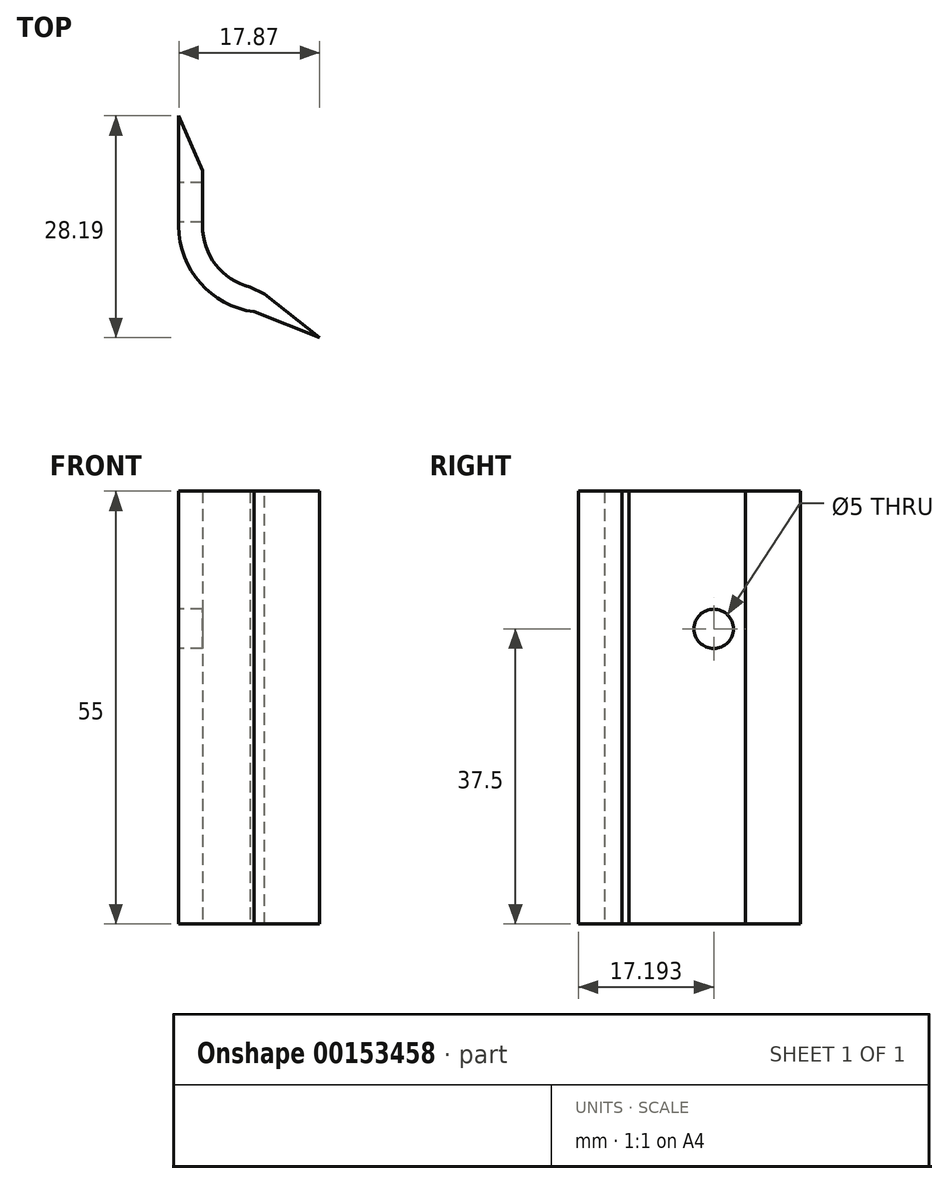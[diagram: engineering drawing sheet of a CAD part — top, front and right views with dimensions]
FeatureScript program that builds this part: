
annotation { "Feature Type Name" : "Feature", "Feature Type Description" : "" }
export const myFeature = defineFeature(function(context is Context, id is Id, definition is map)
    precondition{}
    {
        {
            var Q0;
            Q0=qCreatedBy(makeId("Top.planeOp"),FACE);
            var sketch = newSketch(context, id + "F0", { "sketchPlane" : qUnion([Q0])});
            skLineSegment(sketch, "E0", {"start": v(-60.03, 83.64) * mm, "end": v(-60.03, -26.36) * mm});
            skLineSegment(sketch, "E1", {"start": v(-48.72, -39.25) * mm, "end": v(66.28, -54.25) * mm});
            skLineSegment(sketch, "E2", {"start": v(66.28, -34.25) * mm, "end": v(-0.03, 83.64) * mm});
            skLineSegment(sketch, "E3", {"start": v(-60.03, 83.64) * mm, "end": v(-0.03, 83.64) * mm});
            skLineSegment(sketch, "E4", {"start": v(66.28, -34.25) * mm, "end": v(66.28, -54.25) * mm});
            skPoint(sketch, "E5.visualSharp", {"position": v(-60.03, -37.77) * mm});
            skArc(sketch, "E5.filletArc", {"start": v(-60.03, -26.36) * mm, "mid": v(-56.8, -34.93) * mm, "end": v(-48.72, -39.25) * mm});
            skCircle(sketch, "E6", {"center": v(62.28, -55.74) * mm, "radius": 4 * mm});
            skLineSegment(sketch, "E7", {"start": v(66.28, -55.79) * mm, "end": v(66.28, -54.25) * mm});
            skLineSegment(sketch, "E8", {"start": v(58.37, -54.91) * mm, "end": v(58.59, -53.24) * mm});
            skSolve(sketch);
        }
        {
            var Q0;
            Q0=qSketchRegion(id+"F0",true);
            var Q1;
            {var subQ0=sQuery(id+"F0.wireOp",EDGE,"E6");var subQ1=sQuery(id+"F0.wireOp",EDGE,"E1");var subQ2=makeQuery(id+"F0.imprint","INTERSECT",VERTEX,{"disambiguationData":[OD(0.0)],"derivedFrom":[subQ1,subQ0]});Q1=makeQuery(id+"F0.imprint","IMPRINT",FACE,{"disambiguationData":[TD([[makeQuery(id+"F0.imprint","IMPRINT",EDGE,{"disambiguationData":[TD([[subQ2,-1.0]])],"derivedFrom":subQ1}),1.0]])]});}
            extrude(context, id + "F1", {"entities" : qUnion([Q0, Q1]), "depth" : 4 * mm});
        }
        {
            var Q0;
            Q0=makeQuery(id+"F1.opExtrude","CAP_FACE",FACE,{"disambiguationData":[OSD([sQuery(id+"F0.wireOp",EDGE,"E0"),sQuery(id+"F0.wireOp",EDGE,"E1"),sQuery(id+"F0.wireOp",EDGE,"E2"),sQuery(id+"F0.wireOp",EDGE,"E3"),sQuery(id+"F0.wireOp",EDGE,"E4"),sQuery(id+"F0.wireOp",EDGE,"E5.filletArc")])],"isStart":false});
            var sketch = newSketch(context, id + "F2", { "sketchPlane" : qUnion([Q0])});
            skLineSegment(sketch, "E9.0", {"start": v(-48.46, -37.26) * mm, "end": v(52.4, -50.42) * mm});
            skArc(sketch, "E9.1", {"start": v(-58.03, -26.36) * mm, "mid": v(-55.3, -33.61) * mm, "end": v(-48.46, -37.26) * mm});
            skLineSegment(sketch, "E9.2", {"start": v(-58.03, 83.64) * mm, "end": v(-58.03, -26.36) * mm});
            skLineSegment(sketch, "E10", {"start": v(66.28, -54.25) * mm, "end": v(66.28, -52.23) * mm});
            skLineSegment(sketch, "E11", {"start": v(-60.03, 83.64) * mm, "end": v(-58.03, 83.64) * mm});
            skLineSegment(sketch, "E12", {"start": v(-48.46, -37.26) * mm, "end": v(-48.72, -39.25) * mm});
            skLineSegment(sketch, "E13.0", {"start": v(59.2, -25.73) * mm, "end": v(-2.7, 84.31) * mm});
            skLineSegment(sketch, "E14", {"start": v(-2.33, 83.64) * mm, "end": v(-2.7, 84.31) * mm});
            skLineSegment(sketch, "E15", {"start": v(59.2, -25.73) * mm, "end": v(66.28, -34.25) * mm});
            skSolve(sketch);
        }
        {
            var Q0;
            Q0=qSketchRegion(id+"F2",true);
            var Q1;
            Q1=makeQuery(id+"F2.imprint","IMPRINT",FACE,{"disambiguationData":[TD([[makeQuery(id+"F2.imprint","IMPRINT",EDGE,{"derivedFrom":sQuery(id+"F2.wireOp",EDGE,"E9.1")}),-1.0]])]});
            var Q2;
            {var subQ2=sQuery(id+"F2.wireOp",EDGE,"E14");Q2=makeQuery(id+"F2.imprint","IMPRINT",FACE,{"disambiguationData":[TD([[makeQuery(id+"F2.imprint","IMPRINT",EDGE,{"derivedFrom":subQ2}),-1.0]])]});}
            var Q3;
            {var subQ0=sQuery(id+"F2.wireOp",EDGE,"E13.0");Q3=makeQuery(id+"F2.imprint","IMPRINT",FACE,{"disambiguationData":[TD([[makeQuery(id+"F2.imprint","IMPRINT",EDGE,{"derivedFrom":subQ0}),-1.0]])]});}
            extrude(context, id + "F3", {"entities" : qUnion([Q0, Q1, Q2, Q3]), "operationType" : NewBodyOperationType.ADD, "depth" : 55 * mm});
        }
        {
            var Q0;
            {var subQ0=sQuery(id+"F0.wireOp",EDGE,"E0");Q0=makeQuery(id+"F3.boolean.opBoolean","MERGE",FACE,{"derivedFrom":[makeQuery(id+"F1.opExtrude","SWEPT_FACE",FACE,{"disambiguationData":[OSD([subQ0])]}),makeQuery(id+"F3.opExtrude","SWEPT_FACE",FACE,{"disambiguationData":[OSD([subQ0])]})]});}
            var sketch = newSketch(context, id + "F4", { "sketchPlane" : qUnion([Q0])});
            skCircle(sketch, "E16", {"center": v(23.36, 41.5) * mm, "radius": 2.5 * mm});
            skCircle(sketch, "E17", {"center": v(-74.64, 41.5) * mm, "radius": 2.5 * mm});
            skSolve(sketch);
        }
        {
            var Q0;
            Q0=qSketchRegion(id+"F4",true);
            extrude(context, id + "F5", {"entities" : qUnion([Q0]), "operationType" : NewBodyOperationType.REMOVE, "endBound" : BoundingType.UP_TO_NEXT, "oppositeDirection" : true, "depth" : 25 * mm});
        }
        {
            var Q0;
            Q0=makeQuery(id+"F1.opExtrude","SWEPT_FACE",FACE,{"disambiguationData":[OSD([sQuery(id+"F0.wireOp",EDGE,"E1")])]});
            extrude(context, id + "F6", {"entities" : qUnion([Q0]), "operationType" : NewBodyOperationType.ADD, "depth" : 25 * mm});
        }
        {
            var Q0;
            {var subQ0=sQuery(id+"F0.wireOp",EDGE,"E1");Q0=makeQuery(id+"F6.boolean.opBoolean","MERGE",FACE,{"derivedFrom":[makeQuery(id+"F1.opExtrude","CAP_FACE",FACE,{"disambiguationData":[OSD([sQuery(id+"F0.wireOp",EDGE,"E0"),subQ0,sQuery(id+"F0.wireOp",EDGE,"E2"),sQuery(id+"F0.wireOp",EDGE,"E3"),sQuery(id+"F0.wireOp",EDGE,"E4"),sQuery(id+"F0.wireOp",EDGE,"E5.filletArc"),sQuery(id+"F0.wireOp",EDGE,"E6"),sQuery(id+"F0.wireOp",EDGE,"E7"),sQuery(id+"F0.wireOp",EDGE,"E8")])],"isStart":false}),makeQuery(id+"F6.opExtrude","SWEPT_FACE",FACE,{"disambiguationData":[OSD([subQ0]),TDD([makeQuery(id+"F1.opExtrude","CAP_EDGE",EDGE,{"disambiguationData":[OSD([subQ0])],"isStart":false})])]})]});}
            var sketch = newSketch(context, id + "F7", { "sketchPlane" : qUnion([Q0])});
            skArc(sketch, "E18.0", {"start": v(-55.03, -26.36) * mm, "mid": v(-53.05, -31.64) * mm, "end": v(-48.07, -34.29) * mm});
            skLineSegment(sketch, "E18.1", {"start": v(-55.03, 83.64) * mm, "end": v(-55.03, -26.36) * mm});
            skLineSegment(sketch, "E19", {"start": v(-58.03, -12.36) * mm, "end": v(-55.03, -12.36) * mm});
            skLineSegment(sketch, "E20", {"start": v(-48.72, -39.25) * mm, "end": v(58.29, -55.54) * mm});
            skLineSegment(sketch, "E21", {"start": v(-48.46, -37.26) * mm, "end": v(-40.16, -40.55) * mm});
            skLineSegment(sketch, "E22", {"start": v(-40.16, -40.55) * mm, "end": v(-48.07, -34.29) * mm});
            skSolve(sketch);
        }
        {
            var Q0;
            {var subQ2=sQuery(id+"F7.wireOp",EDGE,"E18.0");Q0=makeQuery(id+"F7.imprint","IMPRINT",FACE,{"disambiguationData":[TD([[makeQuery(id+"F7.imprint","IMPRINT",EDGE,{"derivedFrom":subQ2}),-1.0]])]});}
            extrude(context, id + "F8", {"entities" : qUnion([Q0]), "operationType" : NewBodyOperationType.ADD, "depth" : 55 * mm});
        }
        {
            var Q0;
            Q0=makeQuery(id+"F8.opExtrude","SWEPT_FACE",FACE,{"disambiguationData":[OSD([sQuery(id+"F2.wireOp",EDGE,"E9.2")])]});
            extrude(context, id + "F9", {"entities" : qUnion([Q0]), "operationType" : NewBodyOperationType.REMOVE, "endBound" : BoundingType.UP_TO_NEXT, "oppositeDirection" : true, "depth" : 25 * mm});
        }
        {
            var Q0;
            {var subQ0=sQuery(id+"F2.wireOp",EDGE,"E9.2");var subQ1=sQuery(id+"F2.wireOp",EDGE,"E9.1");Q0=makeQuery(id+"F8.boolean.opBoolean","MERGE",FACE,{"derivedFrom":[makeQuery(id+"F3.opExtrude","CAP_FACE",FACE,{"disambiguationData":[OSD([sQuery(id+"F0.wireOp",EDGE,"E0"),sQuery(id+"F0.wireOp",EDGE,"E5.filletArc"),subQ1,subQ0,sQuery(id+"F2.wireOp",EDGE,"E11"),sQuery(id+"F2.wireOp",EDGE,"E12")])],"isStart":false}),makeQuery(id+"F8.opExtrude","CAP_FACE",FACE,{"disambiguationData":[OSD([subQ1,subQ0,sQuery(id+"F7.wireOp",EDGE,"E18.0"),sQuery(id+"F7.wireOp",EDGE,"E18.1"),sQuery(id+"F7.wireOp",EDGE,"E19"),sQuery(id+"F7.wireOp",EDGE,"E21"),sQuery(id+"F7.wireOp",EDGE,"E22")])],"isStart":false})]});}
            var sketch = newSketch(context, id + "F10", { "sketchPlane" : qUnion([Q0])});
            skArc(sketch, "E23.0", {"start": v(-58.03, -26.36) * mm, "mid": v(-55.3, -33.61) * mm, "end": v(-48.46, -37.26) * mm});
            skLineSegment(sketch, "E23.1", {"start": v(-58.03, 83.64) * mm, "end": v(-58.03, -26.36) * mm});
            skSolve(sketch);
        }
        {
            var Q0;
            Q0=makeQuery(id+"F8.opExtrude","SWEPT_EDGE",EDGE,{"disambiguationData":[OSD([sQuery(id+"F7.wireOp",EDGE,"E18.1"),sQuery(id+"F7.wireOp",EDGE,"E19")])]});
            chamfer(context, id + "F11", {"entities" : qUnion([Q0]), "chamferType" : ChamferType.TWO_OFFSETS, "width1" : 3 * mm, "oppositeDirection" : false, "width2" : 7 * mm, "tangentPropagation" : true});
        }
        {
            var Q0;
            {var subQ3=sQuery(id+"F10.wireOp",EDGE,"E23.0");Q0=makeQuery(id+"F10.imprint","IMPRINT",FACE,{"disambiguationData":[TD([[makeQuery(id+"F10.imprint","IMPRINT",EDGE,{"derivedFrom":subQ3}),-1.0]])]});}
            var Q1;
            Q1=makeQuery(id+"F3.opExtrude","CAP_FACE",FACE,{"disambiguationData":[OSD([sQuery(id+"F0.wireOp",EDGE,"E2"),sQuery(id+"F0.wireOp",EDGE,"E3"),sQuery(id+"F2.wireOp",EDGE,"E13.0"),sQuery(id+"F2.wireOp",EDGE,"E15")])],"isStart":false});
            extrude(context, id + "F12", {"entities" : qUnion([Q0, Q1]), "operationType" : NewBodyOperationType.REMOVE, "oppositeDirection" : true, "depth" : 55 * mm});
        }
        {
            var Q0;
            Q0=makeQuery(id+"F8.opExtrude","SWEPT_EDGE",EDGE,{"disambiguationData":[OSD([sQuery(id+"F7.wireOp",EDGE,"E18.0"),sQuery(id+"F7.wireOp",EDGE,"E22")])]});
            chamfer(context, id + "F13", {"entities" : qUnion([Q0]), "width" : 5 * mm, "tangentPropagation" : true});
        }
        {
            var Q0;
            {var subQ0=sQuery(id+"F0.wireOp",EDGE,"E1");Q0=makeQuery(id+"F6.boolean.opBoolean","MERGE",FACE,{"derivedFrom":[makeQuery(id+"F1.opExtrude","CAP_FACE",FACE,{"disambiguationData":[OSD([sQuery(id+"F0.wireOp",EDGE,"E0"),subQ0,sQuery(id+"F0.wireOp",EDGE,"E2"),sQuery(id+"F0.wireOp",EDGE,"E3"),sQuery(id+"F0.wireOp",EDGE,"E4"),sQuery(id+"F0.wireOp",EDGE,"E5.filletArc"),sQuery(id+"F0.wireOp",EDGE,"E6"),sQuery(id+"F0.wireOp",EDGE,"E7"),sQuery(id+"F0.wireOp",EDGE,"E8")])],"isStart":true}),makeQuery(id+"F6.opExtrude","SWEPT_FACE",FACE,{"disambiguationData":[OSD([subQ0]),TDD([makeQuery(id+"F1.opExtrude","CAP_EDGE",EDGE,{"disambiguationData":[OSD([subQ0])],"isStart":true})])]})]});}
            extrude(context, id + "F14", {"entities" : qUnion([Q0]), "operationType" : NewBodyOperationType.REMOVE, "oppositeDirection" : true, "depth" : 4 * mm});
        }
    });
